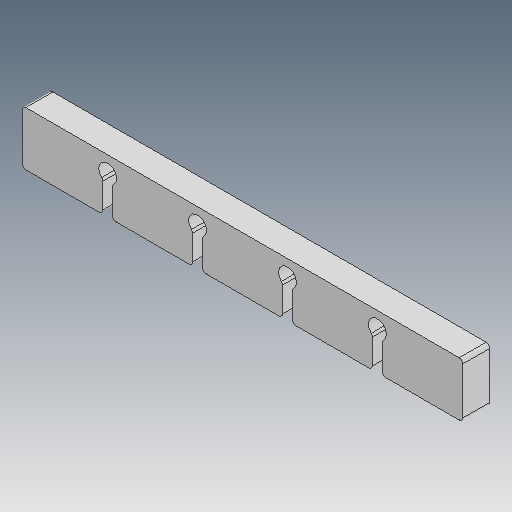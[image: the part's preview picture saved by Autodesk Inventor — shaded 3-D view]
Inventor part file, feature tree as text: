
AUTODESK INVENTOR PART (.ipt)
format: ipt  version: 2020 (Build 240168000, 168)  size: 153,088 bytes
history: native  units: mm
features: extrude x1, sketch x1
ambient origin geometry x8: Origin, YZ Plane, XZ Plane, XY Plane, X Axis, Y Axis, Z Axis, Center Point
bodies: Solid1 (feature_tree)
feature tree (2):
  extrude  "Extrusion1"  Depth=30.0mm
  sketch  "Sketch1"  dims[d0=245.0mm d1=30.0mm d2=10.0mm d3=25.0mm d4=6.0mm d5=5.5mm d6=2.0mm d7=2.0mm d9=10.0mm d10=5.5mm d11=2.0mm d12=2.0mm d13=2.0mm d14=50.0mm d15=15.0mm d16=0.0mm]
